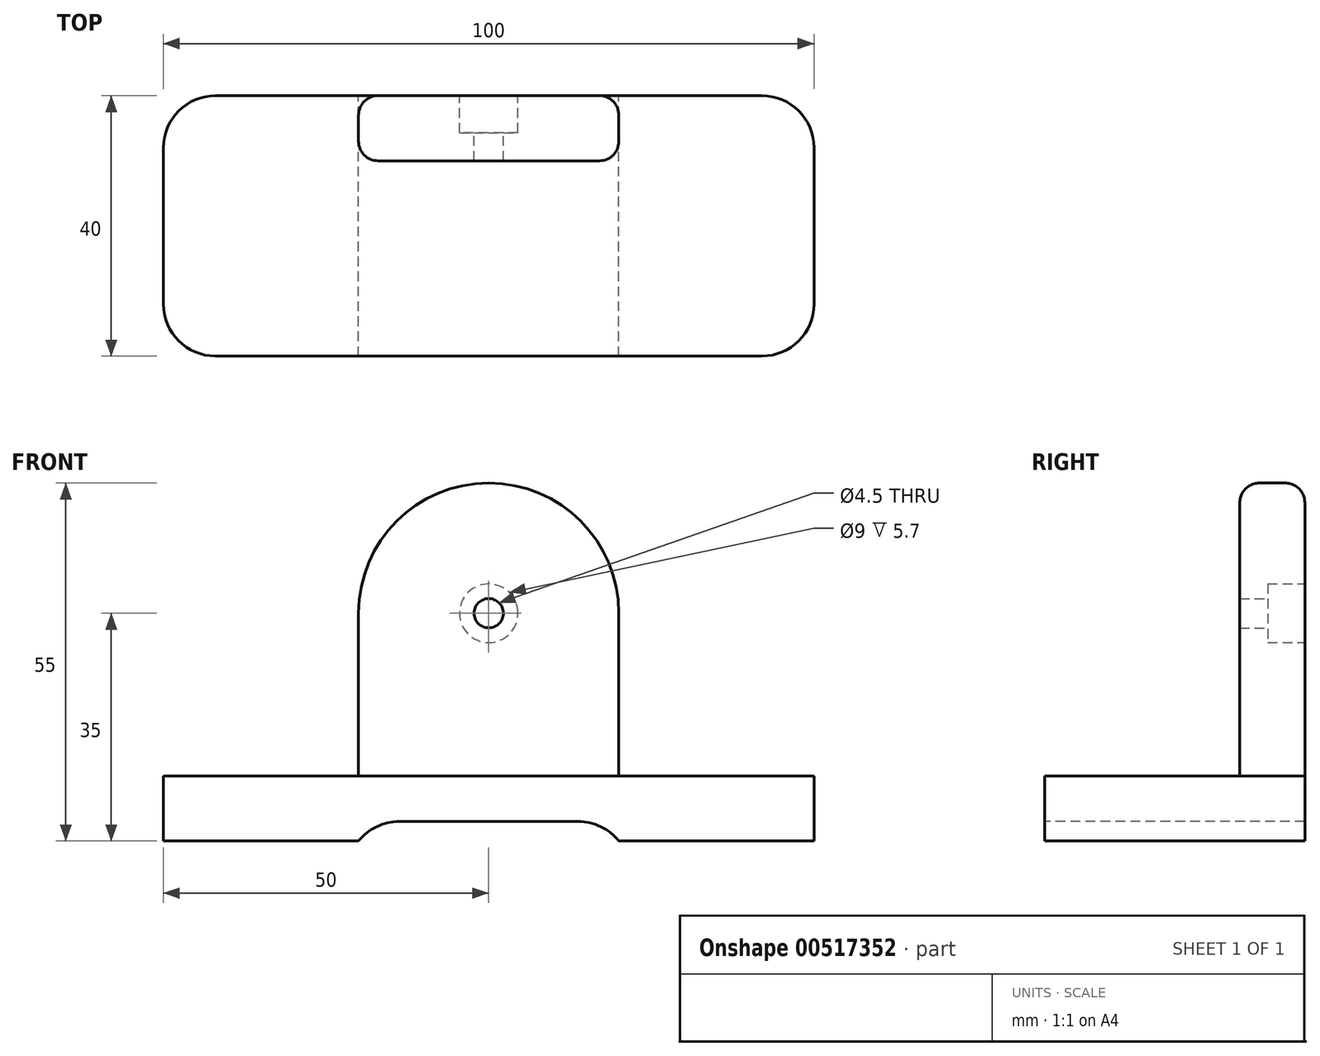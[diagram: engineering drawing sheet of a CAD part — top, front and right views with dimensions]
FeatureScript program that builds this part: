
annotation { "Feature Type Name" : "Feature", "Feature Type Description" : "" }
export const myFeature = defineFeature(function(context is Context, id is Id, definition is map)
    precondition{}
    {
        {
            var Q0;
            Q0=qCreatedBy(makeId("Top.planeOp"),FACE);
            var sketch = newSketch(context, id + "F0", { "sketchPlane" : qUnion([Q0])});
            skLineSegment(sketch, "E0.bottom", {"start": v(0, 0) * mm, "end": v(100, 0) * mm});
            skLineSegment(sketch, "E0.top", {"start": v(0, 40) * mm, "end": v(100, 40) * mm});
            skLineSegment(sketch, "E0.left", {"start": v(0, 0) * mm, "end": v(0, 40) * mm});
            skLineSegment(sketch, "E0.right", {"start": v(100, 0) * mm, "end": v(100, 40) * mm});
            skSolve(sketch);
        }
        {
            var Q0;
            Q0 = qSketchRegion(id + "F0", true);
            extrude(context, id + "F1", {"entities" : qUnion([Q0]), "depth" : 10 * mm, "offsetDistance" : 25 * mm});
        }
        {
            var Q0;
            Q0=makeQuery(id+"F1.opExtrude","SWEPT_FACE",FACE,{"disambiguationData":[OSD([sQuery(id+"F0.wireOp",EDGE,"E0.top")])]});
            var sketch = newSketch(context, id + "F2", { "sketchPlane" : qUnion([Q0])});
            skSolve(sketch);
        }
        {
            var Q0;
            {var subQ0=sQuery(id+"F0.wireOp",EDGE,"E0.top");Q0=makeQuery(id+"F2.imprint","IMPRINT",FACE,{"disambiguationData":[TD([[makeQuery(id+"F2.imprint","IMPRINT",EDGE,{"derivedFrom":makeQuery(id+"F1.opExtrude","CAP_EDGE",EDGE,{"disambiguationData":[OSD([subQ0])],"isStart":true})}),-1.0]])]});}
            var sketch = newSketch(context, id + "F3", { "sketchPlane" : qUnion([Q0])});
            skLineSegment(sketch, "E1", {"start": v(-70, 0) * mm, "end": v(-70, 35) * mm});
            skArc(sketch, "E2", {"start": v(-70, 35) * mm, "mid": v(-50, 55) * mm, "end": v(-30, 35) * mm});
            skLineSegment(sketch, "E3", {"start": v(-30, 35) * mm, "end": v(-30, 0) * mm});
            skLineSegment(sketch, "E4", {"start": v(-30, 0) * mm, "end": v(-70, 0) * mm});
            skSolve(sketch);
        }
        {
            var Q0;
            Q0 = qSketchRegion(id + "F3", true);
            extrude(context, id + "F4", {"entities" : qUnion([Q0]), "operationType" : NewBodyOperationType.ADD, "oppositeDirection" : true, "depth" : 10 * mm, "offsetDistance" : 25 * mm});
        }
        {
            var Q0;
            Q0=makeQuery(id+"F4.boolean.opBoolean","MERGE",FACE,{"derivedFrom":[makeQuery(id+"F1.opExtrude","SWEPT_FACE",FACE,{"disambiguationData":[OSD([sQuery(id+"F0.wireOp",EDGE,"E0.top")])]}),makeQuery(id+"F4.opExtrude","CAP_FACE",FACE,{"disambiguationData":[OSD([sQuery(id+"F3.wireOp",EDGE,"E1"),sQuery(id+"F3.wireOp",EDGE,"E2"),sQuery(id+"F3.wireOp",EDGE,"E3"),sQuery(id+"F3.wireOp",EDGE,"E4")])],"isStart":true})]});
            var sketch = newSketch(context, id + "F5", { "sketchPlane" : qUnion([Q0])});
            skLineSegment(sketch, "E5.bottom", {"start": v(-70, 0) * mm, "end": v(-30, 0) * mm});
            skLineSegment(sketch, "E5.top", {"start": v(-70, 3) * mm, "end": v(-30, 3) * mm});
            skLineSegment(sketch, "E5.left", {"start": v(-70, 0) * mm, "end": v(-70, 3) * mm});
            skLineSegment(sketch, "E5.right", {"start": v(-30, 0) * mm, "end": v(-30, 3) * mm});
            skSolve(sketch);
        }
        {
            var Q0;
            Q0 = qSketchRegion(id + "F5", true);
            extrude(context, id + "F6", {"entities" : qUnion([Q0]), "operationType" : NewBodyOperationType.REMOVE, "endBound" : BoundingType.THROUGH_ALL, "oppositeDirection" : true, "depth" : 25 * mm, "offsetDistance" : 25 * mm});
        }
        {
            var Q0;
            Q0=makeQuery(id+"F4.boolean.opBoolean","MERGE",FACE,{"derivedFrom":[makeQuery(id+"F1.opExtrude","SWEPT_FACE",FACE,{"disambiguationData":[OSD([sQuery(id+"F0.wireOp",EDGE,"E0.top")])]}),makeQuery(id+"F4.opExtrude","CAP_FACE",FACE,{"disambiguationData":[OSD([sQuery(id+"F3.wireOp",EDGE,"E1"),sQuery(id+"F3.wireOp",EDGE,"E2"),sQuery(id+"F3.wireOp",EDGE,"E3"),sQuery(id+"F3.wireOp",EDGE,"E4")])],"isStart":true})]});
            var sketch = newSketch(context, id + "F7", { "sketchPlane" : qUnion([Q0])});
            skCircle(sketch, "E6", {"center": v(-50, 35) * mm, "radius": 2.25 * mm});
            skSolve(sketch);
        }
        {
            var Q0;
            Q0 = qSketchRegion(id + "F7", true);
            extrude(context, id + "F8", {"entities" : qUnion([Q0]), "operationType" : NewBodyOperationType.REMOVE, "endBound" : BoundingType.THROUGH_ALL, "oppositeDirection" : true, "depth" : 25 * mm, "offsetDistance" : 25 * mm});
        }
        {
            var Q0;
            Q0=makeQuery(id+"F4.boolean.opBoolean","MERGE",FACE,{"derivedFrom":[makeQuery(id+"F1.opExtrude","SWEPT_FACE",FACE,{"disambiguationData":[OSD([sQuery(id+"F0.wireOp",EDGE,"E0.top")])]}),makeQuery(id+"F4.opExtrude","CAP_FACE",FACE,{"disambiguationData":[OSD([sQuery(id+"F3.wireOp",EDGE,"E1"),sQuery(id+"F3.wireOp",EDGE,"E2"),sQuery(id+"F3.wireOp",EDGE,"E3"),sQuery(id+"F3.wireOp",EDGE,"E4")])],"isStart":true})]});
            var sketch = newSketch(context, id + "F9", { "sketchPlane" : qUnion([Q0])});
            skCircle(sketch, "E7", {"center": v(-50, 35) * mm, "radius": 4.5 * mm});
            skSolve(sketch);
        }
        {
            var Q0;
            Q0 = qSketchRegion(id + "F9", true);
            extrude(context, id + "F10", {"entities" : qUnion([Q0]), "operationType" : NewBodyOperationType.REMOVE, "oppositeDirection" : true, "depth" : 5.7 * mm, "offsetDistance" : 25 * mm});
        }
        {
            var Q0;
            Q0=makeQuery(id+"F6.boolean.opBoolean","COPY",EDGE,{"derivedFrom":makeQuery(id+"F6.opExtrude","SWEPT_EDGE",EDGE,{"disambiguationData":[OSD([sQuery(id+"F5.wireOp",EDGE,"E5.top"),sQuery(id+"F5.wireOp",EDGE,"E5.left")])]})});
            var Q1;
            Q1=makeQuery(id+"F6.boolean.opBoolean","COPY",EDGE,{"derivedFrom":makeQuery(id+"F6.opExtrude","SWEPT_EDGE",EDGE,{"disambiguationData":[OSD([sQuery(id+"F5.wireOp",EDGE,"E5.top"),sQuery(id+"F5.wireOp",EDGE,"E5.right")])]})});
            var Q2;
            Q2=makeQuery(id+"F1.opExtrude","SWEPT_EDGE",EDGE,{"disambiguationData":[OSD([sQuery(id+"F0.wireOp",EDGE,"E0.top"),sQuery(id+"F0.wireOp",EDGE,"E0.left")])]});
            var Q3;
            Q3=makeQuery(id+"F1.opExtrude","SWEPT_EDGE",EDGE,{"disambiguationData":[OSD([sQuery(id+"F0.wireOp",EDGE,"E0.top"),sQuery(id+"F0.wireOp",EDGE,"E0.right")])]});
            var Q4;
            Q4=makeQuery(id+"F1.opExtrude","SWEPT_EDGE",EDGE,{"disambiguationData":[OSD([sQuery(id+"F0.wireOp",EDGE,"E0.bottom"),sQuery(id+"F0.wireOp",EDGE,"E0.right")])]});
            var Q5;
            Q5=makeQuery(id+"F1.opExtrude","SWEPT_EDGE",EDGE,{"disambiguationData":[OSD([sQuery(id+"F0.wireOp",EDGE,"E0.bottom"),sQuery(id+"F0.wireOp",EDGE,"E0.left")])]});
            fillet(context, id + "F11", {"entities" : qUnion([Q0, Q1, Q2, Q3, Q4, Q5]), "radius" : 8 * mm, "tangentPropagation" : true, "allowEdgeOverflow" : false});
        }
        {
            var Q0;
            Q0=makeQuery(id+"F4.opExtrude","CAP_EDGE",EDGE,{"disambiguationData":[OSD([sQuery(id+"F3.wireOp",EDGE,"E2")])],"isStart":true});
            var Q1;
            Q1=makeQuery(id+"F4.opExtrude","CAP_EDGE",EDGE,{"disambiguationData":[OSD([sQuery(id+"F3.wireOp",EDGE,"E2")])],"isStart":false});
            fillet(context, id + "F12", {"entities" : qUnion([Q0, Q1]), "radius" : 3 * mm, "tangentPropagation" : true, "allowEdgeOverflow" : false});
        }
    });
